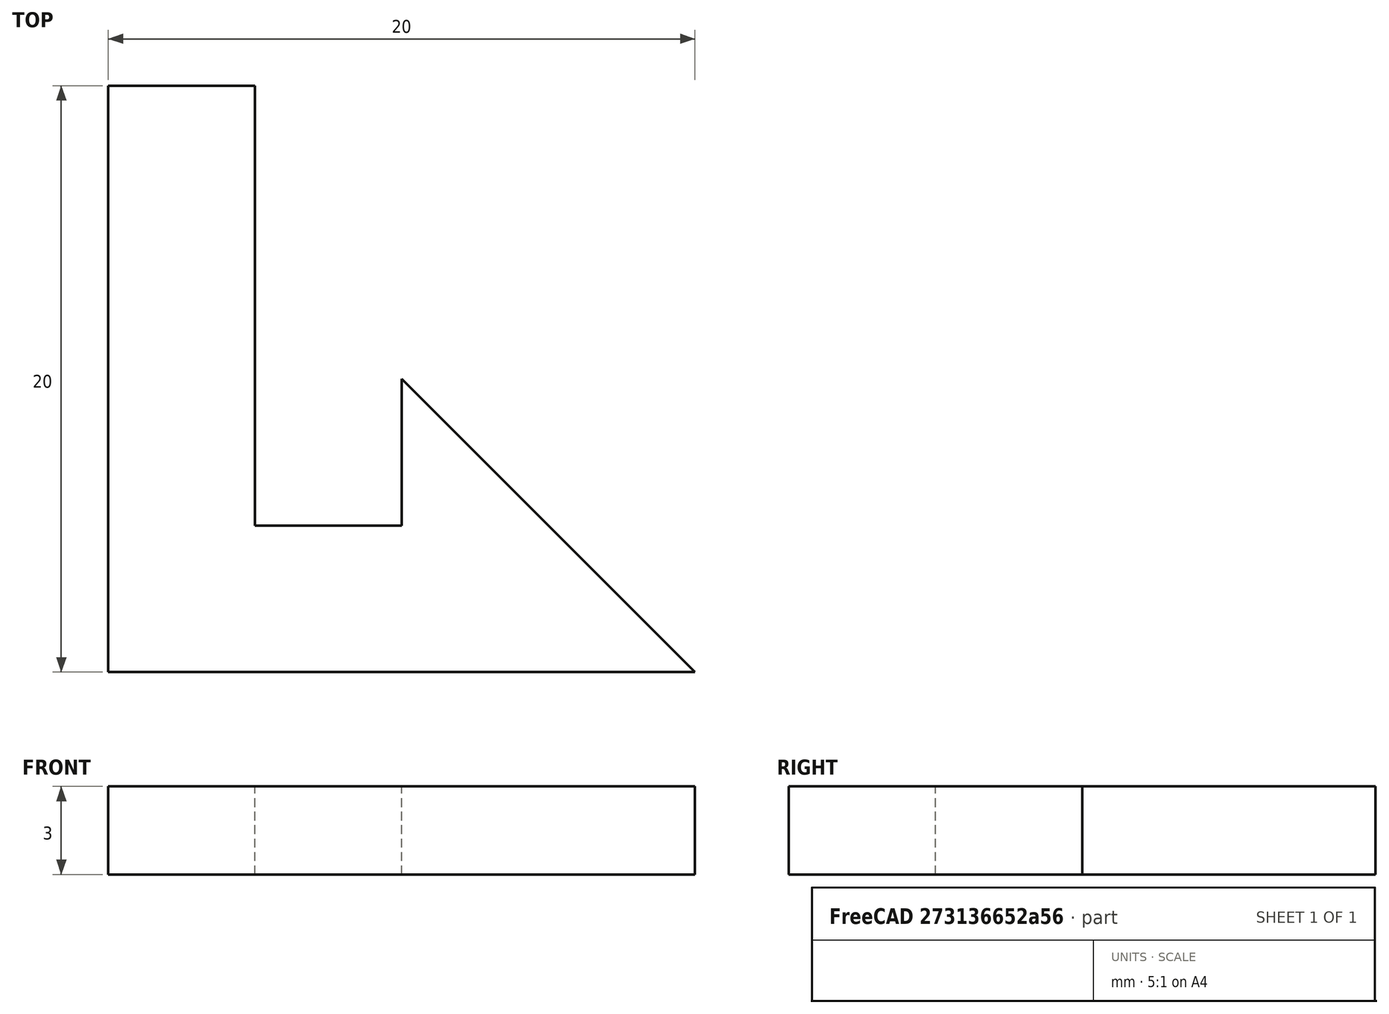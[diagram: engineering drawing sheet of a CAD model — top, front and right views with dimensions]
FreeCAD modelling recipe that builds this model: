
FCSTD DOCUMENT  (FreeCAD 1.0R39109 (Git))
Label: axis_test_arrow
License: All rights reserved
LicenseURL: https://en.wikipedia.org/wiki/All_rights_reserved
objects: Sketcher::SketchObject×1, PartDesign::Pad×1, PartDesign::Body×1
note: 6 computed .brp shape members not serialized (recipe doc carries the construction recipe); baked Part::Feature solids carry a one-line shape summary decoded from their .brp

FEATURE [Sketcher::SketchObject] Sketch
  ArcFitTolerance = 1e-06
  AttachmentSupport = -> [XY_Plane]
  FullyConstrained = true
  MakeInternals = false
  MapMode = 5
  sketch-geometry (7):
    g0: LineSegment StartX=0 StartY=0 StartZ=0 EndX=0 EndY=20 EndZ=0
    g1: LineSegment StartX=0 StartY=20 StartZ=0 EndX=5 EndY=20 EndZ=0
    g2: LineSegment StartX=5 StartY=20 StartZ=0 EndX=5 EndY=5 EndZ=0
    g3: LineSegment StartX=5 StartY=5 StartZ=0 EndX=10 EndY=5 EndZ=0
    g4: LineSegment StartX=10 StartY=5 StartZ=0 EndX=10 EndY=10 EndZ=0
    g5: LineSegment StartX=10 StartY=10 StartZ=0 EndX=20 EndY=0 EndZ=0
    g6: LineSegment StartX=20 StartY=0 StartZ=0 EndX=0 EndY=0 EndZ=0
  constraints (20):
    c: Coincident(g-1,g0)
    c: PointOnObject(g0,g-2)
    c: Coincident(g0,g1)
    c: Coincident(g1,g2)
    c: Vertical(g2)
    c: Coincident(g2,g3)
    c: Horizontal(g3)
    c: Coincident(g3,g4)
    c: Vertical(g4)
    c: Coincident(g4,g5)
    c: PointOnObject(g5,g-1)
    c: Coincident(g5,g6)
    c: Coincident(g6,g0)
    c: Distance(g6,g3) = 5
    c: Distance(g0,g2) = 5
    c: Horizontal(g1)
    c: Distance(g4,g4) = 5
    c: DistanceX(g6,g6) = 20
    c: DistanceY(g0,g0) = 20
    c: Angle(g5,g6) = 0.785398
FEATURE [PartDesign::Pad] Pad
  Direction = (0,0,1)
  Length = 3
  Length2 = 10
  Profile = -> Sketch
  ReferenceAxis = -> Sketch [N_Axis]
  Refine = true
  Suppressed = false
  Type = 0
FEATURE [PartDesign::Body] Body
  AllowCompound = false
  Group = -> [Sketch,Pad]
  Origin = -> Origin
  Tip = -> Pad
